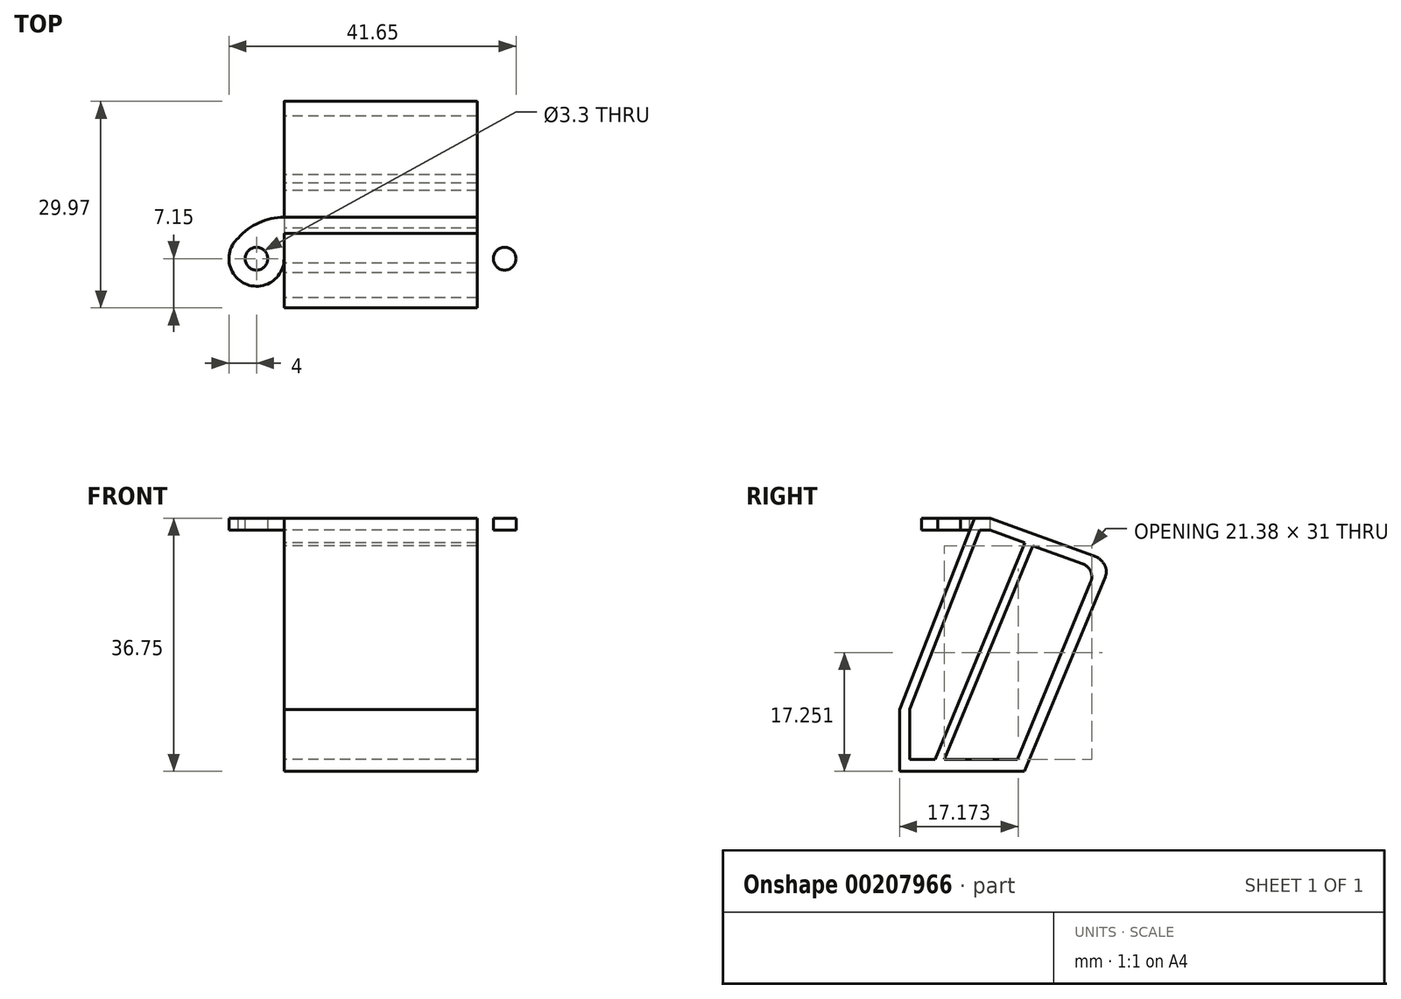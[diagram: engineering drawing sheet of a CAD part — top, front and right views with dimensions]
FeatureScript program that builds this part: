
annotation { "Feature Type Name" : "Feature", "Feature Type Description" : "" }
export const myFeature = defineFeature(function(context is Context, id is Id, definition is map)
    precondition{}
    {
        {
            var Q0;
            Q0=qCreatedBy(makeId("Right.planeOp"),FACE);
            var sketch = newSketch(context, id + "F0", { "sketchPlane" : qUnion([Q0])});
            skLineSegment(sketch, "E0", {"start": v(0, 0) * mm, "end": v(0, 35) * mm, "construction": true});
            skLineSegment(sketch, "E1", {"start": v(0, 35) * mm, "end": v(-3, 35) * mm});
            skLineSegment(sketch, "E2", {"start": v(-3, 35) * mm, "end": v(-3, 36.75) * mm});
            skLineSegment(sketch, "E3", {"start": v(-3, 36.75) * mm, "end": v(0, 36.75) * mm});
            skLineSegment(sketch, "E4.MirrorCS", {"start": v(3, 36.75) * mm, "end": v(0, 36.75) * mm});
            skLineSegment(sketch, "E5.MirrorCS", {"start": v(1.45, 35) * mm, "end": v(3, 35) * mm});
            skPoint(sketch, "E6.startSnap0", {"position": v(0, 17.5) * mm});
            skLineSegment(sketch, "E7", {"start": v(3, 35) * mm, "end": v(16.4, 30.12) * mm});
            skLineSegment(sketch, "E8", {"start": v(3, 36.75) * mm, "end": v(18.04, 31.28) * mm});
            skLineSegment(sketch, "E9", {"start": v(18.04, 29.53) * mm, "end": v(19.91, 28.84) * mm, "construction": true});
            skLineSegment(sketch, "E10", {"start": v(19.66, 28.24) * mm, "end": v(7.96, 0) * mm});
            skPoint(sketch, "E11.visualSharp", {"position": v(18.04, 29.53) * mm});
            skArc(sketch, "E11.filletArc", {"start": v(17.56, 27.48) * mm, "mid": v(17.55, 29.05) * mm, "end": v(16.4, 30.12) * mm});
            skPoint(sketch, "E12.visualSharp", {"position": v(19.91, 28.84) * mm});
            skArc(sketch, "E12.filletArc", {"start": v(19.66, 28.24) * mm, "mid": v(19.81, 29.12) * mm, "end": v(19.56, 29.98) * mm});
            skLineSegment(sketch, "E13", {"start": v(0, 35) * mm, "end": v(-10.15, 9) * mm});
            skLineSegment(sketch, "E14", {"start": v(-10.15, 0) * mm, "end": v(-10.15, 9) * mm});
            skLineSegment(sketch, "E15", {"start": v(1.45, 35) * mm, "end": v(-8.69, 9.03) * mm});
            skPoint(sketch, "E16.orphan", {"position": v(0, 35) * mm});
            skLineSegment(sketch, "E17", {"start": v(7.96, 0) * mm, "end": v(-10.15, 0) * mm});
            skArc(sketch, "E18", {"start": v(19.56, 29.98) * mm, "mid": v(18.91, 30.77) * mm, "end": v(18.04, 31.28) * mm});
            skLineSegment(sketch, "E19", {"start": v(2.7, 0) * mm, "end": v(2.7, 1.75) * mm, "construction": true});
            skLineSegment(sketch, "E20", {"start": v(17.56, 27.48) * mm, "end": v(6.9, 1.75) * mm});
            skLineSegment(sketch, "E21", {"start": v(6.9, 1.75) * mm, "end": v(-8.69, 1.75) * mm});
            skLineSegment(sketch, "E22", {"start": v(-8.69, 1.75) * mm, "end": v(-8.69, 9.03) * mm});
            skLineSegment(sketch, "E23", {"start": v(9.18, 32.75) * mm, "end": v(-3.67, 1.75) * mm});
            skLineSegment(sketch, "E24", {"start": v(8, 33.18) * mm, "end": v(-5.02, 1.75) * mm});
            skSolve(sketch);
        }
        {
            var Q0;
            Q0=makeQuery(id+"F0.imprint","IMPRINT",FACE,{"disambiguationData":[TD([[makeQuery(id+"F0.imprint","IMPRINT",EDGE,{"derivedFrom":sQuery(id+"F0.wireOp",EDGE,"E1")}),-1.0]])]});
            var Q1;
            {var subQ0=sQuery(id+"F0.wireOp",EDGE,"E23");Q1=makeQuery(id+"F0.imprint","IMPRINT",FACE,{"disambiguationData":[TD([[makeQuery(id+"F0.imprint","IMPRINT",EDGE,{"derivedFrom":subQ0}),-1.0]])]});}
            extrude(context, id + "F1", {"entities" : qUnion([Q0, Q1]), "depth" : 28 * mm});
        }
        {
            var Q0;
            Q0=makeQuery(id+"F1.opExtrude","SWEPT_FACE",FACE,{"disambiguationData":[OSD([sQuery(id+"F0.wireOp",EDGE,"E3"),sQuery(id+"F0.wireOp",EDGE,"E4.MirrorCS")])]});
            var sketch = newSketch(context, id + "F2", { "sketchPlane" : qUnion([Q0])});
            skLineSegment(sketch, "E25", {"start": v(14, -3) * mm, "end": v(14, 3) * mm, "construction": true});
            skLineSegment(sketch, "E26", {"start": v(14, 0) * mm, "end": v(-4, 0) * mm, "construction": true});
            skPoint(sketch, "E26.endSnap0", {"position": v(14, 0) * mm});
            skLineSegment(sketch, "E27.MirrorCS", {"start": v(14, 0) * mm, "end": v(32, 0) * mm, "construction": true});
            skCircle(sketch, "E28", {"center": v(-4, -3) * mm, "radius": 1.65 * mm});
            skCircle(sketch, "E29.MirrorC", {"center": v(32, -3) * mm, "radius": 1.65 * mm});
            skArc(sketch, "E30", {"start": v(0, 3) * mm, "mid": v(-3.65, 2.22) * mm, "end": v(-6.65, 0) * mm});
            skArc(sketch, "E31", {"start": v(-3.67, -6.99) * mm, "mid": v(-1.06, -5.71) * mm, "end": v(0, -3) * mm});
            skArc(sketch, "E32.trimOffspring", {"start": v(-6.65, 0) * mm, "mid": v(-7.68, -4.57) * mm, "end": v(-3.67, -6.99) * mm});
            skArc(sketch, "E33.MirrorCS", {"start": v(28, 3) * mm, "mid": v(31.65, 2.22) * mm, "end": v(34.65, 0) * mm});
            skArc(sketch, "E34.MirrorCS", {"start": v(34.65, 0) * mm, "mid": v(35.68, -4.57) * mm, "end": v(31.67, -6.99) * mm});
            skArc(sketch, "E35.MirrorCS", {"start": v(31.67, -6.99) * mm, "mid": v(29.06, -5.71) * mm, "end": v(28, -3) * mm});
            skSolve(sketch);
        }
        {
            var Q0;
            Q0=makeQuery(id+"F2.imprint","IMPRINT",FACE,{"disambiguationData":[TD([[makeQuery(id+"F2.imprint","IMPRINT",EDGE,{"derivedFrom":sQuery(id+"F2.wireOp",EDGE,"E28")}),-1.0]])]});
            var Q1;
            Q1=makeQuery(id+"F2.imprint","IMPRINT",FACE,{"disambiguationData":[TD([[makeQuery(id+"F2.imprint","IMPRINT",EDGE,{"derivedFrom":sQuery(id+"F2.wireOp",EDGE,"E29.MirrorC")}),1.0]])]});
            extrude(context, id + "F3", {"entities" : qUnion([Q0, Q1]), "operationType" : NewBodyOperationType.ADD, "oppositeDirection" : true, "depth" : 1.75 * mm});
        }
        {
            var Q0;
            Q0=makeQuery(id+"F1.opExtrude","SWEPT_FACE",FACE,{"disambiguationData":[OSD([sQuery(id+"F0.wireOp",EDGE,"E2")])]});
            var Q1;
            Q1=makeQuery(id+"F1.opExtrude","SWEPT_FACE",FACE,{"disambiguationData":[OSD([sQuery(id+"F0.wireOp",EDGE,"E13")])]});
            extrude(context, id + "F4", {"entities" : qUnion([Q0]), "operationType" : NewBodyOperationType.REMOVE, "endBound" : BoundingType.UP_TO_SURFACE, "oppositeDirection" : true, "endBoundEntityFace" : qUnion([Q1]), "depth" : 25 * mm});
        }
    });
